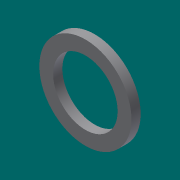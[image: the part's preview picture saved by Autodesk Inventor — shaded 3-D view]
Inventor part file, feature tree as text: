
AUTODESK INVENTOR PART (.ipt)
format: ipt  version: 2013 (Build 170138000, 138)  size: 75,776 bytes
history: native  units: mm
features: other x1, extrude x1, sketch x1
ambient origin geometry x8: Origin, YZ Plane, XZ Plane, XY Plane, X Axis, Y Axis, Z Axis, Center Point
feature tree (3):
  other  "ソリッド1"
  extrude  "押し出し1"  Depth=7.0mm
  sketch  "スケッチ1"
